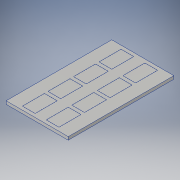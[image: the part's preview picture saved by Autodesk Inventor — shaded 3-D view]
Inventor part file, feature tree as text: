
AUTODESK INVENTOR PART (.ipt)
format: ipt  version: 2019.4 (Build 234330000, 330)  size: 207,360 bytes
history: native  units: in
note: dims shown in document units (in); Inventor stores cm internally (conversion verified against a paired STEP export)
features: extrude x2, sketch x2
ambient origin geometry x8: Origin, YZ Plane, XZ Plane, XY Plane, X Axis, Y Axis, Z Axis, Center Point
bodies: Solid1 (feature_tree)
feature tree (4):
  extrude  "Extrusion1"  Depth=8.5in
  extrude  "Extrusion6"  Depth=1.7717in
  sketch  "Sketch1"  dims[d0=5.0in d1=8.5in]
  sketch  "Sketch7"  dims[d2=0.25in d3=0.0in d76=1.7717in d77=1.0236in d78=0.2835in d79=1.03in d80=0.0197in d81=1.5748in d83=2.0551in d84=0.7874in d86=1.9157in d89=0.0039in d90=0.0in d91=1.0306in]
